# Revit family: Bottle_Filler-Murdock-H2O-To-Go-BF11S
name_source: partatom
category: Plumbing Fixtures
units: mm (PartAtom-declared; Revit-internal decimal feet)

## family parameters
Cut with Voids When Loaded = Yes
Host = Face
OmniClass Number = 23.65.70.14.11
OmniClass Title = Drinking Fountains/Coolers
Part Type = Normal
Room Calculation Point = No
Round Connector Dimension = Use Diameter
Shared = Yes

## types (1)
- BF11S
    -EG22 Enviro-Glaze® Matte Black Powder Coat = No
    -WF1 1500-Gallon Capacity Water Filter1 = No
    -WF3000 3000-Gallon PFAS Water Filter1 = No
    ADA Compliant = Yes
    Assembly Code = D2010820
    CW Connection = Yes
    CWFU = 1.5
    Cold Water Connection Diameter = 3/8"
    Cold Water Connection Height = 19 3/8"
    Cold Water Connection Radius = 3/16"
    Cold Water Connection Width = 2"
    Default Elevation = 0"
    Description = Deck-Mounted SpringH2O® Pushbutton All-Stainless Steel Water Bottle Filling Station - A17 Series Add-On, ADA
    Flow Rate = 1.2 GPM (4.54 l/min) at 70 PSI
    HW Connection = No
    HWFU = 1.5
    Height = 18 1/8"
    Housing Material = Stainless Steel-Murdock-Satin
    IAPMO Compliance = IAPMO tested to NSF/ANSI 61, Section 9, Lead-Free Federal Law 111-380
    Installation Type = Wall Mounted
    Length = 18 1/8"
    Manufacturer = Murdock Mfg.
    Material = Stainless Steel-Murdock-Satin
    Model = BF11S
    Product Documentation Link = https://www.murdockmfg.com
    Product Page URL = https://www.murdockmfg.com
    Type Comments = Bottle filler - hemispherical pushbutton
    URL = https://www.murdockmfg.com
    Vent Connection = No
    WFU = 2
    Waste Connection = No
    Width = 4 3/8"

## geometry (parser evidence)
native form markers: Sweep x3
no freeform markers — native parametric forms only
